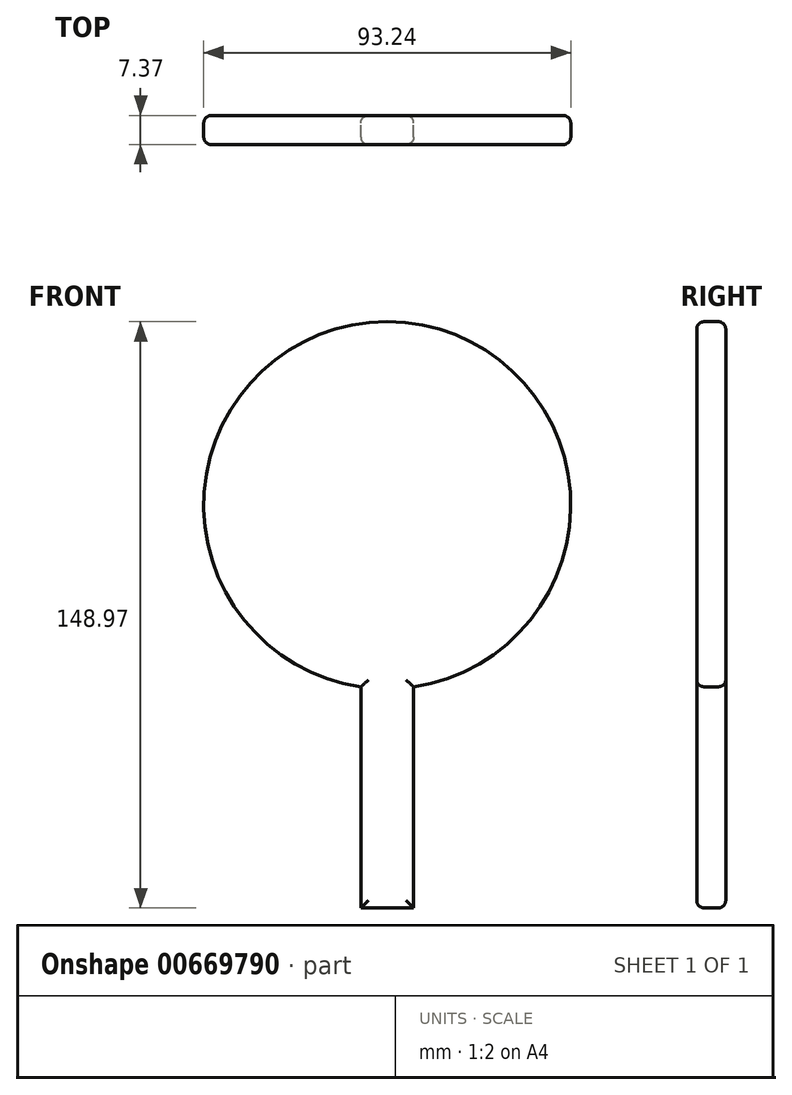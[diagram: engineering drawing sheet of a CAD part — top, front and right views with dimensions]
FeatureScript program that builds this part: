
annotation { "Feature Type Name" : "Feature", "Feature Type Description" : "" }
export const myFeature = defineFeature(function(context is Context, id is Id, definition is map)
    precondition{}
    {
        {
            var Q0;
            Q0=qCreatedBy(makeId("Front.planeOp"),FACE);
            var sketch = newSketch(context, id + "F0", { "sketchPlane" : qUnion([Q0])});
            skArc(sketch, "E0", {"start": v(6.72, -11.96) * mm, "mid": v(0, 80.8) * mm, "end": v(-6.72, -11.96) * mm});
            skLineSegment(sketch, "E1.bottom", {"start": v(6.72, -68.17) * mm, "end": v(-6.72, -68.17) * mm});
            skLineSegment(sketch, "E1.left", {"start": v(6.72, -68.17) * mm, "end": v(6.72, -11.96) * mm});
            skLineSegment(sketch, "E1.right", {"start": v(-6.72, -68.17) * mm, "end": v(-6.72, -11.96) * mm});
            skPoint(sketch, "E1.middle", {"position": v(0, -37.79) * mm});
            skPoint(sketch, "E1.top.end.orphan", {"position": v(-6.72, -7.4) * mm});
            skPoint(sketch, "E1.top.start.orphan", {"position": v(6.72, -7.4) * mm});
            skSolve(sketch);
        }
        {
            var Q0;
            Q0 = qSketchRegion(id + "F0", true);
            extrude(context, id + "F1", {"entities" : qUnion([Q0]), "depth" : 7.37 * mm, "offsetDistance" : 25.4 * mm});
        }
        {
            var Q0;
            Q0=makeQuery(id+"F1.opExtrude","CAP_FACE",FACE,{"disambiguationData":[OSD([sQuery(id+"F0.wireOp",EDGE,"E0"),sQuery(id+"F0.wireOp",EDGE,"E1.bottom"),sQuery(id+"F0.wireOp",EDGE,"E1.left"),sQuery(id+"F0.wireOp",EDGE,"E1.right")])],"isStart":false});
            var Q1;
            Q1=makeQuery(id+"F1.opExtrude","CAP_FACE",FACE,{"disambiguationData":[OSD([sQuery(id+"F0.wireOp",EDGE,"E0"),sQuery(id+"F0.wireOp",EDGE,"E1.bottom"),sQuery(id+"F0.wireOp",EDGE,"E1.left"),sQuery(id+"F0.wireOp",EDGE,"E1.right")])],"isStart":true});
            fillet(context, id + "F2", {"entities" : qUnion([Q0, Q1]), "radius" : 1.9 * mm, "tangentPropagation" : true, "allowEdgeOverflow" : false});
        }
    });
